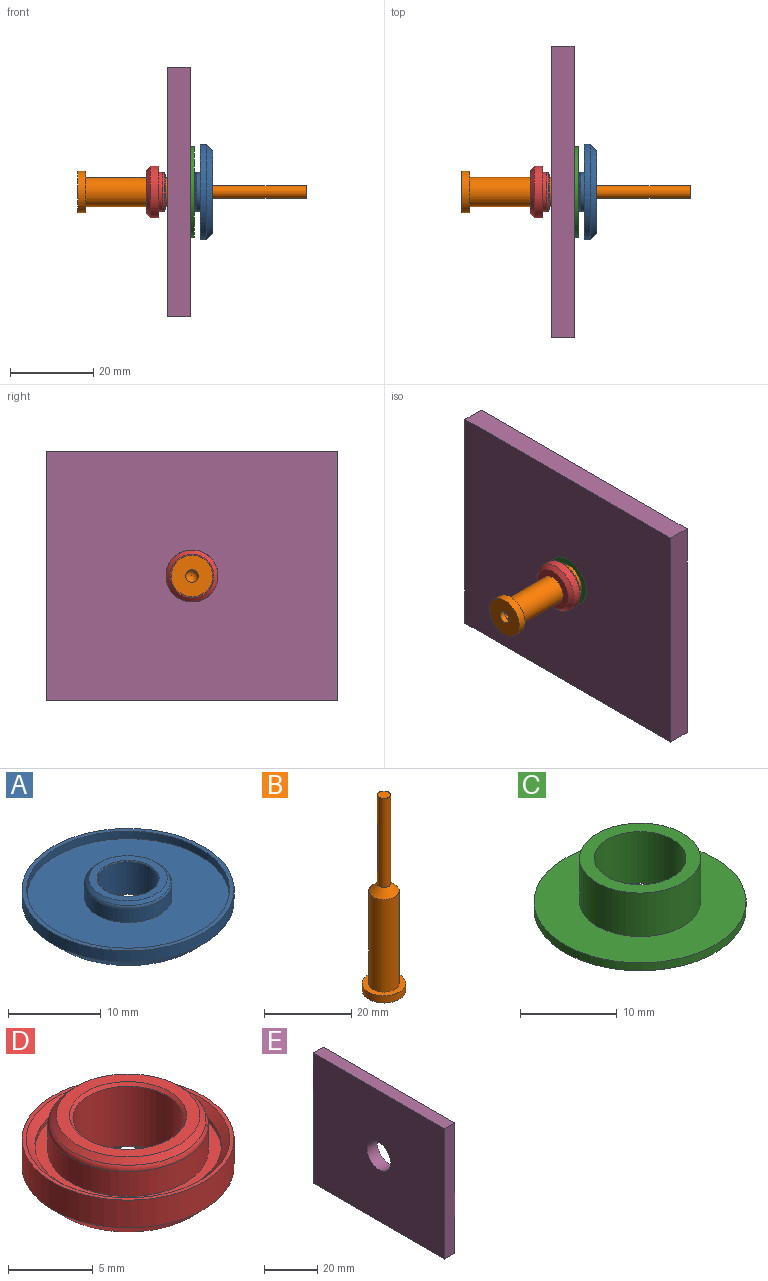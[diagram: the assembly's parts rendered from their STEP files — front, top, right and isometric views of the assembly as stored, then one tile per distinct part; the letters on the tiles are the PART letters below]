
ASSEMBLY  parts=5 mates=5
PART A: 13 faces, bbox 22.9x22.9x4.5 mm
  f0: cylinder r=11.45mm len=22.9mm, axis (0,0,-1), area 107.9mm2, adj f1,f5
  f1: plane 22.9x22.9mm, normal (0,0,1), area 35.2mm2, adj f0,f3
  f2: plane 19.9x19.9mm, normal (0,0,-1), area 275.8mm2, adj f5,f10
  f3: cylinder r=10.95mm len=21.9mm, axis (0,0,1), area 68.8mm2, adj f1,f4
  f4: plane 21.9x21.9mm, normal (0,0,1), area 306.2mm2, adj f3,f6
  f5: cone r=11.45mm half-angle=45deg, axis (0,0,1), area 142.6mm2, adj f0,f2
  f6: cylinder r=4.73mm len=9.47mm, axis (0,0,-1), area 53.3mm2, adj f4,f12
  f7: plane 8.47x8.47mm, normal (0,0,1), area 21.1mm2, adj f8,f11
  f8: cone r=4.24mm half-angle=45deg, axis (0,0,-1), area 13.9mm2, adj f7,f12
  f9: cylinder r=3.25mm len=6.5mm, axis (0,0,1), area 87.8mm2, adj f10,f11
  f10: cone r=3.35mm half-angle=45deg, axis (0,0,-1), area 2.9mm2, adj f2,f9
  f11: cone r=3.25mm half-angle=45deg, axis (0,0,1), area 2.9mm2, adj f7,f9
  f12: torus R=4.24mm, axis (0,0,1), area 11.6mm2, adj f6,f8
PART B: 9 faces, bbox 10x10x55 mm
  f0: cylinder r=5mm len=10mm, axis (0,0,-1), area 62.8mm2, adj f1,f2
  f1: plane 10x10mm, normal (0,0,1), area 40.1mm2, adj f0,f3
  f2: plane 10x10mm, normal (0,0,-1), area 71.5mm2, adj f0,f7
  f3: cylinder r=3.5mm len=26mm, axis (0,0,-1), area 571.8mm2, adj f1,f6
  f4: cylinder r=1.5mm len=25mm, axis (0,0,-1), area 235.6mm2, adj f5,f6
  f5: plane 3x3mm, normal (0,0,1), area 7.1mm2, adj f4
  f6: cone r=1.5mm half-angle=45deg, axis (0,0,-1), area 44.4mm2, adj f3,f4
  f7: cylinder r=1.5mm len=3mm, axis (0,0,-1), area 14.1mm2, adj f2,f8
  f8: sphere r=1.5mm, area 14.1mm2, adj f7
PART C: 6 faces, bbox 21.9x21.9x6.5 mm
  f0: cylinder r=10.95mm len=21.9mm, axis (0,0,-1), area 68.8mm2, adj f1,f2
  f1: plane 21.9x21.9mm, normal (0,0,1), area 254mm2, adj f0,f3
  f2: plane 21.9x21.9mm, normal (0,0,-1), area 306.1mm2, adj f0,f5
  f3: cylinder r=6.25mm len=12.5mm, axis (0,0,-1), area 216mm2, adj f1,f4
  f4: plane 12.5x12.5mm, normal (0,0,1), area 52.1mm2, adj f3,f5
  f5: cylinder r=4.74mm len=9.48mm, axis (0,0,1), area 193.6mm2, adj f2,f4
PART D: 14 faces, bbox 12.5x12.5x4.7 mm
  f0: cylinder r=6.25mm len=12.5mm, axis (0,0,-1), area 78.5mm2, adj f1,f10
  f1: plane 12.5x12.5mm, normal (0,0,1), area 9.6mm2, adj f0,f5
  f2: plane 10.5x10.5mm, normal (0,0,-1), area 49.2mm2, adj f10,f12
  f3: cylinder r=5.5mm len=11mm, axis (0,0,1), area 10.4mm2, adj f4,f5
  f4: plane 11x11mm, normal (0,0,1), area 24.6mm2, adj f3,f6
  f5: cone r=5.5mm half-angle=45deg, axis (0,0,1), area 25.5mm2, adj f1,f3
  f6: cylinder r=4.73mm len=9.47mm, axis (0,0,-1), area 53.3mm2, adj f4,f9
  f7: plane 8.47x8.47mm, normal (0,0,1), area 19mm2, adj f8,f13
  f8: cone r=4.24mm half-angle=45deg, axis (0,0,-1), area 13.9mm2, adj f7,f9
  f9: torus R=4.24mm, axis (0,0,1), area 11.6mm2, adj f6,f8
  f10: cone r=6.25mm half-angle=45deg, axis (0,0,1), area 51.1mm2, adj f0,f2
  f11: cylinder r=3.25mm len=6.5mm, axis (0,0,-1), area 87.8mm2, adj f12,f13
  f12: cone r=3.25mm half-angle=45deg, axis (0,0,-1), area 6mm2, adj f2,f11
  f13: cone r=3.25mm half-angle=45deg, axis (0,0,1), area 6mm2, adj f7,f11
PART E: 7 faces, bbox 5.5x70x60 mm
  f0: plane 70x60mm, normal (-1,0,0), area 4077.3mm2, adj f1,f3,f4,f5,f6
  f1: plane 60x5.5mm, normal (0,-1,0), area 330mm2, adj f0,f2,f4,f5
  f2: plane 70x60mm, normal (1,0,0), area 4077.3mm2, adj f1,f3,f4,f5,f6
  f3: plane 60x5.5mm, normal (0,1,0), area 330mm2, adj f0,f2,f4,f5
  f4: plane 70x5.5mm, normal (0,0,1), area 385mm2, adj f0,f1,f2,f3
  f5: plane 70x5.5mm, normal (0,0,-1), area 385mm2, adj f0,f1,f2,f3
  f6: cylinder r=6.25mm len=12.5mm, axis (-1,0,0), area 216mm2, adj f0,f2
PLACE A rot(axis=(-0.58,-0.58,0.58),120deg) t=(-197.51,-36.75,62.85)mm
PLACE B rot(axis=(0.71,0,0.71),180deg) t=(-229.96,-36.75,62.85)mm
PLACE C rot(axis=(0.71,0,-0.71),180deg) t=(-201.91,-36.75,62.85)mm
PLACE D rot(axis=(0.58,0.58,0.58),120deg) t=(-213.51,-36.75,62.85)mm
PLACE E rot(axis=(0,0,1),180deg) t=(-202.91,-1.75,32.85)mm
MATE cylindrical E.f6 <-> C.f3  axis (1,0,0) through (-205.66,-36.75,62.85)mm
MATE cylindrical C.f5 <-> A.f6  axis (-1,0,0) through (-205.16,-36.75,62.85)mm
MATE cylindrical D.f6 <-> C.f5  axis (-1,0,0) through (-210.41,-36.75,62.85)mm
MATE fastened C.f3 <-> E.f6  axis (-1,0,0) through (-202.91,-36.75,62.85)mm
MATE cylindrical D.f0 <-> B.f3  axis (-1,0,0) through (-213.51,-36.75,62.85)mm
